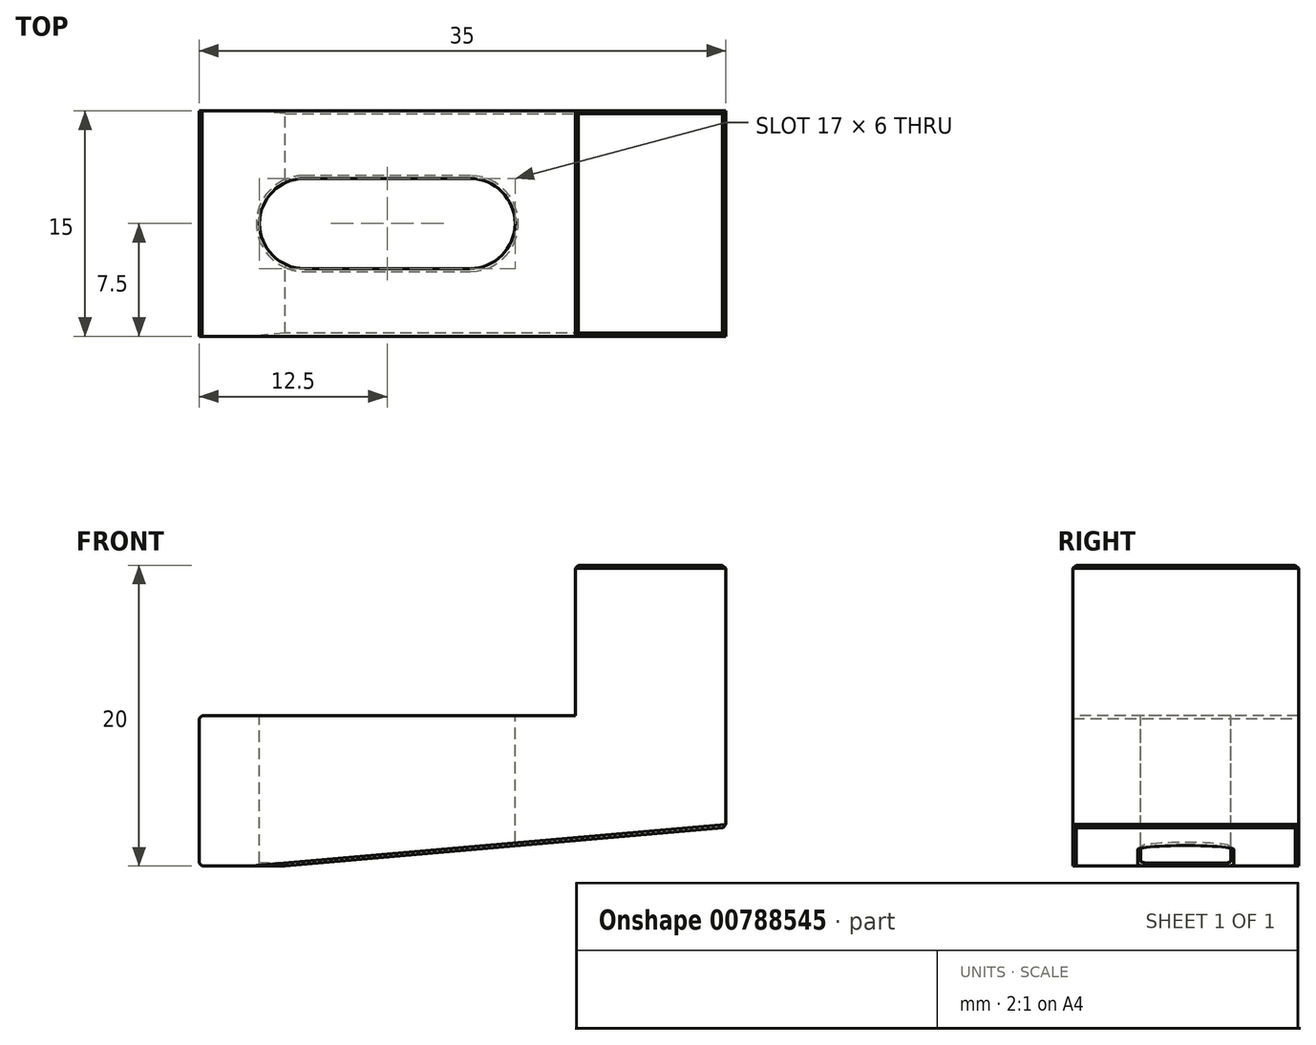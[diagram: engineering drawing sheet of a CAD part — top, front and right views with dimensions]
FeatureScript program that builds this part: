
annotation { "Feature Type Name" : "Feature", "Feature Type Description" : "" }
export const myFeature = defineFeature(function(context is Context, id is Id, definition is map)
    precondition{}
    {
        {
            var Q0;
            Q0=qCreatedBy(makeId("Front.planeOp"),FACE);
            var sketch = newSketch(context, id + "F0", { "sketchPlane" : qUnion([Q0])});
            skLineSegment(sketch, "E0", {"start": v(5.72, 0.5) * mm, "end": v(35, 3.06) * mm});
            skLineSegment(sketch, "E1", {"start": v(35, 3.06) * mm, "end": v(35, 20.5) * mm});
            skLineSegment(sketch, "E2", {"start": v(35, 20.5) * mm, "end": v(25, 20.5) * mm});
            skLineSegment(sketch, "E3", {"start": v(0, 10.5) * mm, "end": v(0, 0.5) * mm});
            skLineSegment(sketch, "E4", {"start": v(3, 10.5) * mm, "end": v(3, 10.5) * mm});
            skLineSegment(sketch, "E5", {"start": v(3, 10.5) * mm, "end": v(25, 10.5) * mm});
            skLineSegment(sketch, "E6", {"start": v(25, 10.5) * mm, "end": v(25, 20.5) * mm});
            skLineSegment(sketch, "E7", {"start": v(0, 0.5) * mm, "end": v(5.72, 0.5) * mm});
            skPoint(sketch, "E8.orphan", {"position": v(0, 0) * mm});
            skLineSegment(sketch, "E9", {"start": v(0, 10.5) * mm, "end": v(3, 10.5) * mm});
            skSolve(sketch);
        }
        {
            var Q0;
            Q0=makeQuery(id+"F0.imprint","IMPRINT",FACE,{"disambiguationData":[TD([[makeQuery(id+"F0.imprint","IMPRINT",EDGE,{"derivedFrom":sQuery(id+"F0.wireOp",EDGE,"E0")}),1.0]])]});
            extrude(context, id + "F1", {"entities" : qUnion([Q0]), "endBound" : BoundingType.SYMMETRIC, "depth" : 15 * mm, "offsetDistance" : 25 * mm});
        }
        {
            var Q0;
            Q0=makeQuery(id+"F1.opExtrude","SWEPT_FACE",FACE,{"disambiguationData":[OSD([sQuery(id+"F0.wireOp",EDGE,"E5")])]});
            var sketch = newSketch(context, id + "F2", { "sketchPlane" : qUnion([Q0])});
            skLineSegment(sketch, "E10", {"start": v(25, 0) * mm, "end": v(25, 0) * mm});
            skArc(sketch, "E11", {"start": v(7, 3) * mm, "mid": v(4, 0) * mm, "end": v(7, -3) * mm});
            skArc(sketch, "E12", {"start": v(18, -3) * mm, "mid": v(21, 0) * mm, "end": v(18, 3) * mm});
            skLineSegment(sketch, "E13", {"start": v(7, 3) * mm, "end": v(18, 3) * mm});
            skLineSegment(sketch, "E14", {"start": v(7, -3) * mm, "end": v(18, -3) * mm});
            skSolve(sketch);
        }
        {
            var Q0;
            Q0=makeQuery(id+"F2.imprint","IMPRINT",FACE,{"disambiguationData":[TD([[makeQuery(id+"F2.imprint","IMPRINT",EDGE,{"derivedFrom":sQuery(id+"F2.wireOp",EDGE,"MUn7YBft-WoBk-3efg-pGZN-NsojyXTX8tUo")}),1.0]])]});
            var Q1;
            Q1=makeQuery(id+"F2.imprint","IMPRINT",FACE,{"disambiguationData":[TD([[makeQuery(id+"F2.imprint","IMPRINT",EDGE,{"derivedFrom":sQuery(id+"F2.wireOp",EDGE,"E11")}),1.0]])]});
            extrude(context, id + "F3", {"entities" : qUnion([Q0, Q1]), "operationType" : NewBodyOperationType.REMOVE, "endBound" : BoundingType.THROUGH_ALL, "oppositeDirection" : true, "depth" : 25 * mm, "offsetDistance" : 25 * mm});
        }
        {
            var Q0;
            Q0=makeQuery(id+"F1.opExtrude","CAP_EDGE",EDGE,{"disambiguationData":[OSD([sQuery(id+"F0.wireOp",EDGE,"855fb9f1-322f-4306-abb0-9ace9ab77bd5.trimOffspring")])],"isStart":false});
            var Q1;
            Q1=makeQuery(id+"F1.opExtrude","SWEPT_EDGE",EDGE,{"disambiguationData":[OSD([sQuery(id+"F0.wireOp",EDGE,"E3"),sQuery(id+"F0.wireOp",EDGE,"855fb9f1-322f-4306-abb0-9ace9ab77bd5.trimOffspring")])]});
            var Q2;
            Q2=makeQuery(id+"F1.opExtrude","CAP_EDGE",EDGE,{"disambiguationData":[OSD([sQuery(id+"F0.wireOp",EDGE,"855fb9f1-322f-4306-abb0-9ace9ab77bd5.trimOffspring")])],"isStart":true});
            var Q3;
            Q3=makeQuery(id+"F1.opExtrude","SWEPT_EDGE",EDGE,{"disambiguationData":[OSD([sQuery(id+"F0.wireOp",EDGE,"E4"),sQuery(id+"F0.wireOp",EDGE,"855fb9f1-322f-4306-abb0-9ace9ab77bd5.trimOffspring")])]});
            var Q4;
            Q4=makeQuery(id+"F1.opExtrude","SWEPT_EDGE",EDGE,{"disambiguationData":[OSD([sQuery(id+"F0.wireOp",EDGE,"E2"),sQuery(id+"F0.wireOp",EDGE,"E6")])]});
            var Q5;
            Q5=makeQuery(id+"F1.opExtrude","CAP_EDGE",EDGE,{"disambiguationData":[OSD([sQuery(id+"F0.wireOp",EDGE,"E2")])],"isStart":false});
            var Q6;
            Q6=makeQuery(id+"F1.opExtrude","SWEPT_EDGE",EDGE,{"disambiguationData":[OSD([sQuery(id+"F0.wireOp",EDGE,"E1"),sQuery(id+"F0.wireOp",EDGE,"E2")])]});
            var Q7;
            Q7=makeQuery(id+"F1.opExtrude","CAP_EDGE",EDGE,{"disambiguationData":[OSD([sQuery(id+"F0.wireOp",EDGE,"E2")])],"isStart":true});
            var Q8;
            Q8=makeQuery(id+"F3.boolean.opBoolean","COPY",EDGE,{"derivedFrom":makeQuery(id+"F3.opExtrude","CAP_EDGE",EDGE,{"disambiguationData":[OSD([sQuery(id+"F2.wireOp",EDGE,"E13")])],"isStart":true})});
            var Q9;
            Q9=makeQuery(id+"F1.opExtrude","CAP_EDGE",EDGE,{"disambiguationData":[OSD([sQuery(id+"F0.wireOp",EDGE,"E0")])],"isStart":false});
            var Q10;
            Q10=makeQuery(id+"F1.opExtrude","SWEPT_EDGE",EDGE,{"disambiguationData":[OSD([sQuery(id+"F0.wireOp",EDGE,"E0"),sQuery(id+"F0.wireOp",EDGE,"E1")])]});
            var Q11;
            Q11=makeQuery(id+"F1.opExtrude","CAP_EDGE",EDGE,{"disambiguationData":[OSD([sQuery(id+"F0.wireOp",EDGE,"E0")])],"isStart":true});
            var Q12;
            Q12=makeQuery(id+"F1.opExtrude","SWEPT_EDGE",EDGE,{"disambiguationData":[OSD([sQuery(id+"F0.wireOp",EDGE,"E3"),sQuery(id+"F0.wireOp",EDGE,"E7")])]});
            var Q13;
            Q13=makeQuery(id+"F3.boolean.opBoolean","INTERSECT",EDGE,{"derivedFrom":[makeQuery(id+"F1.opExtrude","SWEPT_FACE",FACE,{"disambiguationData":[OSD([sQuery(id+"F0.wireOp",EDGE,"E0")])]}),makeQuery(id+"F3.opExtrude","SWEPT_FACE",FACE,{"disambiguationData":[OSD([sQuery(id+"F2.wireOp",EDGE,"E13")])]})]});
            chamfer(context, id + "F4", {"entities" : qUnion([Q0, Q1, Q2, Q3, Q4, Q5, Q6, Q7, Q8, Q9, Q10, Q11, Q12, Q13]), "width" : 0.2 * mm, "tangentPropagation" : true});
        }
        {
            var Q0;
            Q0=makeQuery(id+"F1.opExtrude","SWEPT_BODY",BODY,{"disambiguationData":[OSD([sQuery(id+"F0.wireOp",EDGE,"E0"),sQuery(id+"F0.wireOp",EDGE,"E1"),sQuery(id+"F0.wireOp",EDGE,"E2"),sQuery(id+"F0.wireOp",EDGE,"E3"),sQuery(id+"F0.wireOp",EDGE,"E4"),sQuery(id+"F0.wireOp",EDGE,"E5"),sQuery(id+"F0.wireOp",EDGE,"E6"),sQuery(id+"F0.wireOp",EDGE,"855fb9f1-322f-4306-abb0-9ace9ab77bd5.trimOffspring"),sQuery(id+"F0.wireOp",EDGE,"E7")])]});
            transform(context, id + "F5", {"entities" : qUnion([Q0]), "transformType" : TransformType.TRANSLATION_3D, "dx" : 0 * mm, "dy" : 0 * mm, "dz" : 0 * mm, "makeCopy" : true});
        }
    });
